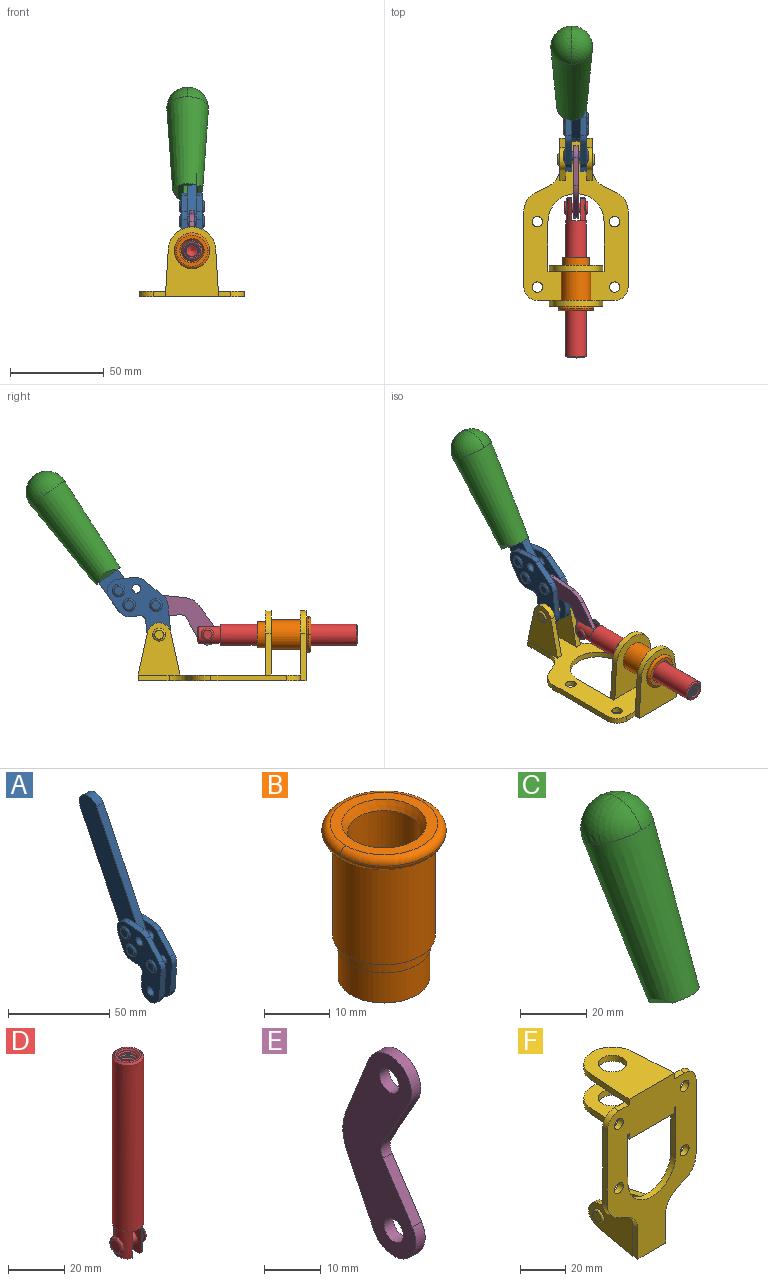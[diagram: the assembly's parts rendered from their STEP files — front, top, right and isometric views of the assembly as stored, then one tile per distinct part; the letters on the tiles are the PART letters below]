
ASSEMBLY  parts=6 mates=6
PART A: 59 faces, bbox 12.9x60.2x99.6 mm
  f0: torus R=2.39mm, axis (-1,0,0), area 14.9mm2, adj f20,f43,f51
  f1: torus R=2.39mm, axis (-1,0,0), area 14.9mm2, adj f19,f42,f51
  f2: torus R=2.39mm, axis (-1,0,0), area 14.9mm2, adj f18,f35,f51
  f3: torus R=2.39mm, axis (-1,0,0), area 14.9mm2, adj f14,f17,f23
  f4: torus R=2.39mm, axis (-1,0,0), area 14.9mm2, adj f13,f16,f23
  f5: torus R=2.39mm, axis (-1,0,0), area 14.9mm2, adj f12,f15,f23
  f6: cylinder r=2.39mm len=4.78mm, axis (1,0,0), area 46.5mm2, adj f48,f50,f51
  f7: cylinder r=2.39mm len=4.78mm, axis (1,0,0), area 46.5mm2, adj f50,f51
  f8: cylinder r=6.35mm len=12.68mm, axis (1,0,0), area 61.8mm2, adj f38,f39,f50,f51
  f9: cylinder r=2.39mm len=4.78mm, axis (-1,0,0), area 70.5mm2, adj f46,f50
  f10: cylinder r=2.39mm len=4.78mm, axis (-1,0,0), area 46.5mm2, adj f23,f45,f46
  f11: cylinder r=2.39mm len=4.78mm, axis (-1,0,0), area 46.5mm2, adj f23,f46
  f12: plane 4.78x4.78mm, normal (1,0,0), area 17.9mm2, adj f5,f15
  f13: plane 4.78x4.78mm, normal (1,0,0), area 17.9mm2, adj f4,f16
  f14: plane 4.78x4.78mm, normal (1,0,0), area 17.9mm2, adj f3,f17
  f15: torus R=2.39mm, axis (-1,0,0), area 14.9mm2, adj f5,f12,f23
  f16: torus R=2.39mm, axis (-1,0,0), area 14.9mm2, adj f4,f13,f23
  f17: torus R=2.39mm, axis (-1,0,0), area 14.9mm2, adj f3,f14,f23
  f18: plane 4.78x4.78mm, normal (-1,0,0), area 17.9mm2, adj f2,f35
  f19: plane 4.78x4.78mm, normal (-1,0,0), area 17.9mm2, adj f1,f42
  f20: plane 4.78x4.78mm, normal (-1,0,0), area 17.9mm2, adj f0,f43
  f21: plane 2.26x0.2mm, normal (1,0,0), area 0.2mm2, adj f31,f44
  f22: plane 2.26x0.2mm, normal (-1,0,0), area 0.2mm2, adj f41,f44
  f23: plane 39.37x30.77mm, normal (1,0,0), area 565.5mm2, adj f3,f4,f5,f10,f11,f15,f16,f17
  f24: cylinder r=6.1mm len=4.15mm, axis (-1,0,0), area 14.7mm2, adj f23,f25,f32,f46
  f25: plane 10.25x9.01mm, normal (0,-0.75,0.66), area 42.3mm2, adj f23,f24,f26,f46
  f26: cylinder r=6.35mm len=4.64mm, axis (-1,0,0), area 15.6mm2, adj f23,f25,f27,f46
  f27: plane 15.84x3.1mm, normal (0,-1,-0.07), area 49.2mm2, adj f23,f26,f28,f46
  f28: cylinder r=6.35mm len=12.68mm, axis (-1,0,0), area 61.8mm2, adj f23,f27,f29,f46
  f29: plane 8.11x3.1mm, normal (0,1,0.07), area 25.2mm2, adj f23,f28,f30,f46
  f30: cylinder r=3.05mm len=3.25mm, axis (-1,0,0), area 14.8mm2, adj f23,f29,f31,f46
  f31: plane 5.99x3.1mm, normal (0,0.07,-1), area 18.6mm2, adj f21,f23,f30,f44,f46
  f32: plane 9.5x3.1mm, normal (0,-0.07,1), area 29.5mm2, adj f23,f24,f33,f46,f47
  f33: cylinder r=6.1mm len=8.63mm, axis (-1,0,0), area 39.1mm2, adj f23,f32,f34,f47
  f34: plane 8.65x3.96mm, normal (0,0.91,-0.42), area 29.5mm2, adj f23,f33,f44,f47
  f35: torus R=2.39mm, axis (-1,0,0), area 14.9mm2, adj f2,f18,f51
  f36: plane 10.25x9.01mm, normal (0,-0.75,0.66), area 42.3mm2, adj f37,f49,f50,f51
  f37: cylinder r=6.35mm len=4.64mm, axis (1,0,0), area 15.6mm2, adj f36,f38,f50,f51
  f38: plane 15.84x3.1mm, normal (0,-1,-0.07), area 49.2mm2, adj f8,f37,f50,f51
  f39: plane 8.11x3.1mm, normal (0,1,0.07), area 25.2mm2, adj f8,f40,f50,f51
  f40: cylinder r=3.05mm len=3.25mm, axis (1,0,0), area 14.8mm2, adj f39,f41,f50,f51
  f41: plane 5.99x3.1mm, normal (0,0.07,-1), area 18.6mm2, adj f22,f40,f44,f50,f51
  f42: torus R=2.39mm, axis (-1,0,0), area 14.9mm2, adj f1,f19,f51
  f43: torus R=2.39mm, axis (-1,0,0), area 14.9mm2, adj f0,f20,f51
  f44: cylinder r=6.35mm len=12.12mm, axis (-1,0,0), area 128.9mm2, adj f21,f22,f23,f31,f34,f41,f46,f47
  f45: plane 2.65x1.35mm, normal (1,0,0), area 1mm2, adj f10,f55
  f46: plane 39.08x20.42mm, normal (-1,0,0), area 412.5mm2, adj f9,f10,f11,f24,f25,f26,f27,f28
  f47: plane 77.62x39.82mm, normal (1,0,0), area 850mm2, adj f32,f33,f34,f44,f53,f54,f55
  f48: plane 2.65x1.35mm, normal (-1,0,0), area 1mm2, adj f6,f55
  f49: cylinder r=6.1mm len=4.15mm, axis (1,0,0), area 14.7mm2, adj f36,f50,f51,f56
  f50: plane 39.08x20.42mm, normal (1,0,0), area 412.5mm2, adj f6,f7,f8,f9,f36,f37,f38,f39
  f51: plane 39.37x30.77mm, normal (-1,0,0), area 565.5mm2, adj f0,f1,f2,f6,f7,f8,f35,f36
  f52: plane 8.65x3.96mm, normal (0,0.91,-0.42), area 29.5mm2, adj f44,f51,f57,f58
  f53: plane 68.49x33.4mm, normal (0,0.9,-0.44), area 358.1mm2, adj f44,f47,f54,f58
  f54: cylinder r=6.35mm len=12.06mm, axis (1,0,0), area 93.7mm2, adj f47,f53,f55,f58
  f55: plane 68.49x33.4mm, normal (0,-0.9,0.44), area 358.1mm2, adj f44,f45,f46,f47,f48,f50,f54,f58
  f56: plane 9.5x3.1mm, normal (0,-0.07,1), area 29.5mm2, adj f49,f50,f51,f57,f58
  f57: cylinder r=6.1mm len=8.63mm, axis (1,0,0), area 39.1mm2, adj f51,f52,f56,f58
  f58: plane 77.62x39.82mm, normal (-1,0,0), area 850mm2, adj f44,f52,f53,f54,f55,f56,f57
PART B: 15 faces, bbox 20.6x20.6x28.7 mm
  f0: torus R=8.26mm, axis (0,0,1), area 56.8mm2, adj f1,f10,f12
  f1: torus R=8.26mm, axis (0,0,1), area 56.8mm2, adj f0,f6,f13
  f2: cylinder r=5.59mm len=25.91mm, axis (0,0,1), area 909.6mm2, adj f3,f4
  f3: cone r=6.86mm half-angle=45deg, axis (0,0,-1), area 70.2mm2, adj f2,f14
  f4: cone r=6.47mm half-angle=30deg, axis (0,0,1), area 66.7mm2, adj f2,f13
  f5: cylinder r=7.04mm len=14.07mm, axis (0,0,1), area 252.6mm2, adj f11,f14
  f6: torus R=8.26mm, axis (0,0,1), area 56.8mm2, adj f1,f12,f13
  f7: cylinder r=7.16mm len=14.33mm, axis (0,0,1), area 91.5mm2, adj f9,f11
  f8: cylinder r=7.86mm len=18.42mm, axis (0,0,1), area 909.6mm2, adj f9,f10
  f9: plane 15.72x15.72mm, normal (0,0,-1), area 33mm2, adj f7,f8
  f10: plane 16.51x16.51mm, normal (0,0,-1), area 19.9mm2, adj f0,f8,f12
  f11: plane 14.33x14.33mm, normal (0,0,-1), area 5.7mm2, adj f5,f7
  f12: torus R=8.26mm, axis (0,0,1), area 56.8mm2, adj f0,f6,f10
  f13: plane 16.51x16.51mm, normal (0,0,1), area 82.7mm2, adj f1,f4,f6
  f14: plane 14.07x14.07mm, normal (0,0,-1), area 7.8mm2, adj f3,f5
PART C: 11 faces, bbox 22.3x42.6x64.5 mm
  f0: sphere r=11.13mm, area 411.4mm2, adj f1,f8
  f1: cone r=11.11mm half-angle=3.3deg, axis (0,0.44,0.9), area 3251.8mm2, adj f0,f7,f8,f9,f10
  f2: cylinder r=6.16mm len=11.7mm, axis (1,0,0), area 89.5mm2, adj f3,f4,f5,f6
  f3: plane 60.23x36.75mm, normal (-1,0,0), area 763.6mm2, adj f2,f4,f6,f10
  f4: plane 51.37x25.05mm, normal (0,0.9,-0.44), area 264.2mm2, adj f2,f3,f5,f10
  f5: plane 60.23x36.75mm, normal (1,0,0), area 763.6mm2, adj f2,f4,f6,f10
  f6: plane 51.37x25.05mm, normal (0,-0.9,0.44), area 264.2mm2, adj f2,f3,f5,f10
  f7: plane 9.95x5.95mm, normal (0.71,-0.31,-0.64), area 25.8mm2, adj f1,f10
  f8: sphere r=11.13mm, area 411.4mm2, adj f0,f1
  f9: plane 9.95x5.95mm, normal (-0.71,-0.31,-0.64), area 25.8mm2, adj f1,f10
  f10: plane 14.27x11.38mm, normal (0,-0.44,-0.9), area 106.7mm2, adj f1,f3,f4,f5,f6,f7,f9
PART D: 48 faces, bbox 12.6x11.1x86.1 mm
  f0: torus R=2.41mm, axis (-1,0,0), area 15mm2, adj f30,f32,f34
  f1: torus R=2.41mm, axis (-1,0,0), area 15mm2, adj f29,f31,f33
  f2: cylinder r=5.54mm len=72.39mm, axis (0,0,1), area 2518.5mm2, adj f3,f4,f42,f43
  f3: cone r=5.54mm half-angle=45deg, axis (0,0,1), area 7.6mm2, adj f2,f5,f41
  f4: cone r=5.54mm half-angle=45deg, axis (0,0,-1), area 34.9mm2, adj f2,f39
  f5: cylinder r=5.08mm len=11.48mm, axis (0,0,1), area 108.3mm2, adj f3,f7,f8,f41
  f6: cylinder r=2.41mm len=4.83mm, axis (-1,0,0), area 71.2mm2, adj f40,f41
  f7: cylinder r=2.41mm len=4.83mm, axis (-1,0,0), area 7.6mm2, adj f5,f34
  f8: cone r=5.08mm half-angle=45deg, axis (0,0,1), area 10.6mm2, adj f5,f37,f41
  f9: cone r=3.98mm half-angle=45deg, axis (0,0,1), area 17.6mm2, adj f27,f39,f45,f46,f47
  f10: cylinder r=2.41mm len=4.83mm, axis (-1,0,0), area 7.6mm2, adj f33,f38
  f11: cylinder r=3.2mm len=6.4mm, axis (0,0,1), area 78.4mm2, adj f12,f28,f44,f45,f47
  f12: cylinder r=3.2mm len=6.4mm, axis (0,0,1), area 10.5mm2, adj f11,f13,f45,f47
  f13: cylinder r=3.2mm len=6.4mm, axis (0,0,1), area 10.5mm2, adj f12,f14,f45,f47
  f14: cylinder r=3.2mm len=6.4mm, axis (0,0,1), area 10.5mm2, adj f13,f15,f45,f47
  f15: cylinder r=3.2mm len=6.4mm, axis (0,0,1), area 10.5mm2, adj f14,f16,f45,f47
  f16: cylinder r=3.2mm len=6.4mm, axis (0,0,1), area 10.5mm2, adj f15,f17,f45,f47
  f17: cylinder r=3.2mm len=6.4mm, axis (0,0,1), area 10.5mm2, adj f16,f18,f45,f47
  f18: cylinder r=3.2mm len=6.4mm, axis (0,0,1), area 10.5mm2, adj f17,f19,f45,f47
  f19: cylinder r=3.2mm len=6.4mm, axis (0,0,1), area 10.5mm2, adj f18,f20,f45,f47
  f20: cylinder r=3.2mm len=6.4mm, axis (0,0,1), area 10.5mm2, adj f19,f21,f45,f47
  f21: cylinder r=3.2mm len=6.4mm, axis (0,0,1), area 10.5mm2, adj f20,f22,f45,f47
  f22: cylinder r=3.2mm len=6.4mm, axis (0,0,1), area 10.5mm2, adj f21,f23,f45,f47
  f23: cylinder r=3.2mm len=6.4mm, axis (0,0,1), area 10.5mm2, adj f22,f24,f45,f47
  f24: cylinder r=3.2mm len=6.4mm, axis (0,0,1), area 10.5mm2, adj f23,f25,f45,f47
  f25: cylinder r=3.2mm len=6.4mm, axis (0,0,1), area 10.5mm2, adj f24,f26,f45,f47
  f26: cylinder r=3.2mm len=6.4mm, axis (0,0,1), area 10.5mm2, adj f25,f27,f45,f47
  f27: cylinder r=3.2mm len=6.4mm, axis (0,0,1), area 7.4mm2, adj f9,f26,f45,f47
  f28: cone r=3.2mm half-angle=60deg, axis (0,0,1), area 37.2mm2, adj f11
  f29: plane 4.83x4.83mm, normal (-1,0,0), area 18.3mm2, adj f1,f31
  f30: plane 4.83x4.83mm, normal (1,0,0), area 18.3mm2, adj f0,f32
  f31: torus R=2.41mm, axis (-1,0,0), area 15mm2, adj f1,f29,f33
  f32: torus R=2.41mm, axis (-1,0,0), area 15mm2, adj f0,f30,f34
  f33: plane 6.83x6.83mm, normal (1,0,0), area 18.3mm2, adj f1,f10,f31
  f34: plane 6.83x6.83mm, normal (-1,0,0), area 18.3mm2, adj f0,f7,f32
  f35: cone r=5.08mm half-angle=45deg, axis (0,0,1), area 10.6mm2, adj f36,f38,f40
  f36: plane 7.25x1.97mm, normal (0,0,-1), area 10mm2, adj f35,f40
  f37: plane 7.25x1.97mm, normal (0,0,-1), area 10mm2, adj f8,f41
  f38: cylinder r=5.08mm len=11.48mm, axis (0,0,1), area 108.3mm2, adj f10,f35,f40,f42
  f39: plane 9.55x9.55mm, normal (0,0,1), area 22mm2, adj f4,f9
  f40: plane 12.76x10.09mm, normal (1,0,0), area 95.7mm2, adj f6,f35,f36,f38,f42,f43
  f41: plane 12.76x10.09mm, normal (-1,0,0), area 95.7mm2, adj f3,f5,f6,f8,f37,f43
  f42: cone r=5.54mm half-angle=45deg, axis (0,0,1), area 7.6mm2, adj f2,f38,f40
  f43: plane 11.07x4.7mm, normal (0,0,-1), area 50.4mm2, adj f2,f40,f41
  f44: plane 0.89x0.62mm, normal (-1,0,0), area 0.3mm2, adj f11,f45,f46,f47
  f45: bspline ~24.8x7.63mm, area 266.6mm2, adj f9,f11,f12,f13,f14,f15,f16,f17
  f46: bspline ~24.87x7.63mm, area 73.6mm2, adj f9,f44,f45,f47
  f47: bspline ~24.98x7.63mm, area 272.5mm2, adj f9,f11,f12,f13,f14,f15,f16,f17
PART E: 12 faces, bbox 2.3x18.2x42.8 mm
  f0: cylinder r=2.4mm len=4.8mm, axis (1,0,0), area 34.9mm2, adj f4,f11
  f1: cylinder r=10.41mm len=8.47mm, axis (1,0,0), area 20.2mm2, adj f4,f9,f10,f11
  f2: cylinder r=3.05mm len=3.16mm, axis (1,0,0), area 7.7mm2, adj f4,f6,f7,f11
  f3: cylinder r=2.4mm len=4.8mm, axis (1,0,0), area 34.9mm2, adj f4,f11
  f4: plane 42.81x18.23mm, normal (-1,0,0), area 414.1mm2, adj f0,f1,f2,f3,f5,f6,f7,f8
  f5: cylinder r=5.54mm len=10.67mm, axis (1,0,0), area 41.8mm2, adj f4,f6,f10,f11
  f6: plane 11.66x6.53mm, normal (0,-0.87,-0.49), area 30.9mm2, adj f2,f4,f5,f11
  f7: plane 11.17x7.33mm, normal (0,-0.84,0.55), area 30.9mm2, adj f2,f4,f8,f11
  f8: cylinder r=5.54mm len=10.51mm, axis (1,0,0), area 41.8mm2, adj f4,f7,f9,f11
  f9: plane 13.67x6.67mm, normal (0,0.9,-0.44), area 35.1mm2, adj f1,f4,f8,f11
  f10: plane 14.1x5.7mm, normal (0,0.93,0.37), area 35.1mm2, adj f1,f4,f5,f11
  f11: plane 42.81x18.23mm, normal (1,0,0), area 414.1mm2, adj f0,f1,f2,f3,f5,f6,f7,f8
PART F: 55 faces, bbox 55.7x37.4x89.8 mm
  f0: torus R=2.41mm, axis (-1,0,0), area 15mm2, adj f11,f15,f25
  f1: torus R=2.41mm, axis (-1,0,0), area 15mm2, adj f10,f12,f22
  f2: cylinder r=2.78mm len=5.56mm, axis (0,-1,0), area 54.2mm2, adj f30,f54
  f3: cylinder r=14.99mm len=29.97mm, axis (0,-1,0), area 145.9mm2, adj f30,f49,f53,f54
  f4: cylinder r=2.78mm len=5.56mm, axis (0,-1,0), area 54.2mm2, adj f30,f54
  f5: cylinder r=2.78mm len=5.56mm, axis (0,-1,0), area 54.2mm2, adj f30,f54
  f6: cylinder r=2.78mm len=5.56mm, axis (0,-1,0), area 54.2mm2, adj f30,f54
  f7: cylinder r=6.35mm len=12.7mm, axis (0,0,1), area 123.6mm2, adj f27,f51
  f8: cylinder r=6.35mm len=12.7mm, axis (0,0,-1), area 124.7mm2, adj f21,f35
  f9: cylinder r=2.41mm len=11.18mm, axis (-1,0,0), area 169.4mm2, adj f16,f19
  f10: plane 4.83x4.83mm, normal (1,0,0), area 18.3mm2, adj f1,f12
  f11: plane 4.83x4.83mm, normal (-1,0,0), area 18.3mm2, adj f0,f15
  f12: torus R=2.41mm, axis (-1,0,0), area 15mm2, adj f1,f10,f22
  f13: cylinder r=6.35mm len=12.41mm, axis (1,0,0), area 53.4mm2, adj f18,f19,f22,f23
  f14: cylinder r=6.35mm len=12.41mm, axis (-1,0,0), area 53.4mm2, adj f16,f17,f24,f25
  f15: torus R=2.41mm, axis (-1,0,0), area 15mm2, adj f0,f11,f25
  f16: plane 27.86x22.35mm, normal (1,0,0), area 425.4mm2, adj f9,f14,f17,f24,f30
  f17: plane 22.86x4.97mm, normal (0,0.21,0.98), area 72.5mm2, adj f14,f16,f25,f30
  f18: plane 22.86x4.97mm, normal (0,0.21,0.98), area 72.5mm2, adj f13,f19,f22,f30
  f19: plane 27.86x22.35mm, normal (-1,0,0), area 425.4mm2, adj f9,f13,f18,f23,f30
  f20: cylinder r=12.7mm len=25.35mm, axis (0,0,-1), area 119.8mm2, adj f21,f34,f35,f36
  f21: plane 34.21x28.07mm, normal (0,0,-1), area 702.4mm2, adj f8,f20,f30,f34,f36
  f22: plane 27.96x22.45mm, normal (1,0,0), area 407.2mm2, adj f1,f12,f13,f18,f23,f30,f42,f43
  f23: plane 22.86x4.97mm, normal (0,0.21,-0.98), area 72.5mm2, adj f13,f19,f22,f44
  f24: plane 22.86x4.97mm, normal (0,0.21,-0.98), area 72.5mm2, adj f14,f16,f25,f44
  f25: plane 27.86x22.35mm, normal (-1,0,0), area 407.1mm2, adj f0,f14,f15,f17,f24,f30,f45,f46
  f26: plane 3.1x0.95mm, normal (0,0,-1), area 2.7mm2, adj f30,f49,f50,f54
  f27: plane 34.21x28.07mm, normal (0,0,1), area 702.4mm2, adj f7,f28,f30,f50,f52
  f28: cylinder r=12.7mm len=25.35mm, axis (0,0,1), area 118.8mm2, adj f27,f50,f51,f52
  f29: plane 3.1x0.95mm, normal (0,0,-1), area 2.7mm2, adj f30,f52,f53,f54
  f30: plane 86.54x55.63mm, normal (0,1,0), area 2362.9mm2, adj f2,f3,f4,f5,f6,f16,f17,f18
  f31: plane 40.56x3.1mm, normal (-1,0,0), area 125.7mm2, adj f30,f32,f48,f54
  f32: cylinder r=7.11mm len=7.11mm, axis (0,-1,0), area 34.6mm2, adj f30,f31,f33,f54
  f33: plane 6.67x3.1mm, normal (0,0,1), area 20.4mm2, adj f30,f32,f34,f54
  f34: plane 25.39x3.13mm, normal (-1,0.06,0), area 79.5mm2, adj f20,f21,f33,f35,f54
  f35: plane 37.31x28.45mm, normal (0,0,1), area 789.9mm2, adj f8,f20,f34,f36,f54
  f36: plane 25.39x3.13mm, normal (1,0.06,0), area 79.5mm2, adj f20,f21,f35,f37,f54
  f37: plane 6.67x3.1mm, normal (0,0,1), area 20.4mm2, adj f30,f36,f38,f54
  f38: cylinder r=7.11mm len=7.11mm, axis (0,-1,0), area 34.6mm2, adj f30,f37,f39,f54
  f39: plane 40.56x3.1mm, normal (1,0,0), area 125.7mm2, adj f30,f38,f40,f54
  f40: cylinder r=11.18mm len=10.16mm, axis (0,-1,0), area 39.5mm2, adj f30,f39,f41,f54
  f41: plane 6.09x3.1mm, normal (0.42,0,-0.91), area 20.8mm2, adj f30,f40,f42,f54
  f42: cylinder r=11.18mm len=9.41mm, axis (0,-1,0), area 37.2mm2, adj f22,f30,f41,f43,f54
  f43: plane 16.5x3.1mm, normal (1,0,0), area 51.1mm2, adj f22,f42,f44,f54
  f44: plane 17.37x3.1mm, normal (0,0,-1), area 53.8mm2, adj f23,f24,f30,f43,f45,f54
  f45: plane 16.5x3.1mm, normal (-1,0,0), area 51.1mm2, adj f25,f44,f46,f54
  f46: cylinder r=11.18mm len=9.41mm, axis (0,-1,0), area 37.2mm2, adj f25,f30,f45,f47,f54
  f47: plane 6.09x3.1mm, normal (-0.42,0,-0.91), area 20.8mm2, adj f30,f46,f48,f54
  f48: cylinder r=11.18mm len=10.16mm, axis (0,-1,0), area 39.5mm2, adj f30,f31,f47,f54
  f49: plane 26.54x3.1mm, normal (-1,0,0), area 82.3mm2, adj f3,f26,f30,f54
  f50: plane 25.39x3.1mm, normal (1,0.06,0), area 78.8mm2, adj f26,f27,f28,f51,f54
  f51: plane 37.31x28.45mm, normal (0,0,-1), area 789.9mm2, adj f7,f28,f50,f52,f54
  f52: plane 25.39x3.1mm, normal (-1,0.06,0), area 78.8mm2, adj f27,f28,f29,f51,f54
  f53: plane 26.54x3.1mm, normal (1,0,0), area 82.3mm2, adj f3,f29,f30,f54
  f54: plane 89.66x55.63mm, normal (0,-1,0), area 2678.5mm2, adj f2,f3,f4,f5,f6,f26,f29,f31
PLACE A rot(axis=(-1,0,0),10deg) t=(0,22.57,60.49)mm
PLACE B rot(axis=(1,0,0),90deg) t=(0,9.14,0)mm
PLACE C rot(axis=(-1,0,0),10deg) t=(-2.31,22.57,60.49)mm
PLACE D rot(axis=(1,0,0),90deg) t=(0,30.82,0)mm
PLACE E rot(axis=(1,0,0),121.8deg) t=(0,41.47,11.86)mm
PLACE F rot(axis=(1,0,0),90deg) t=(0,9.14,0)mm fixed
MATE revolute D.f6 <-> E.f5  axis (-1,0,0) through (0,15.35,24.61)mm
MATE revolute E.f3 <-> A.f4  axis (1,0,0) through (0,42.89,40.4)mm
MATE fastened C.f2 <-> A.f54  axis (-1,0,0) through (0,102.04,102.1)mm
MATE revolute F.f0 <-> A.f7  axis (-1,0,0) through (0,41.23,24.61)mm
MATE slider D.f2 <-> B.f2  axis (0,-1,0) through (0,-27.96,24.61)mm
MATE fastened F.f7 <-> B.f0  axis (0,-1,0) through (0,-37.25,24.61)mm
